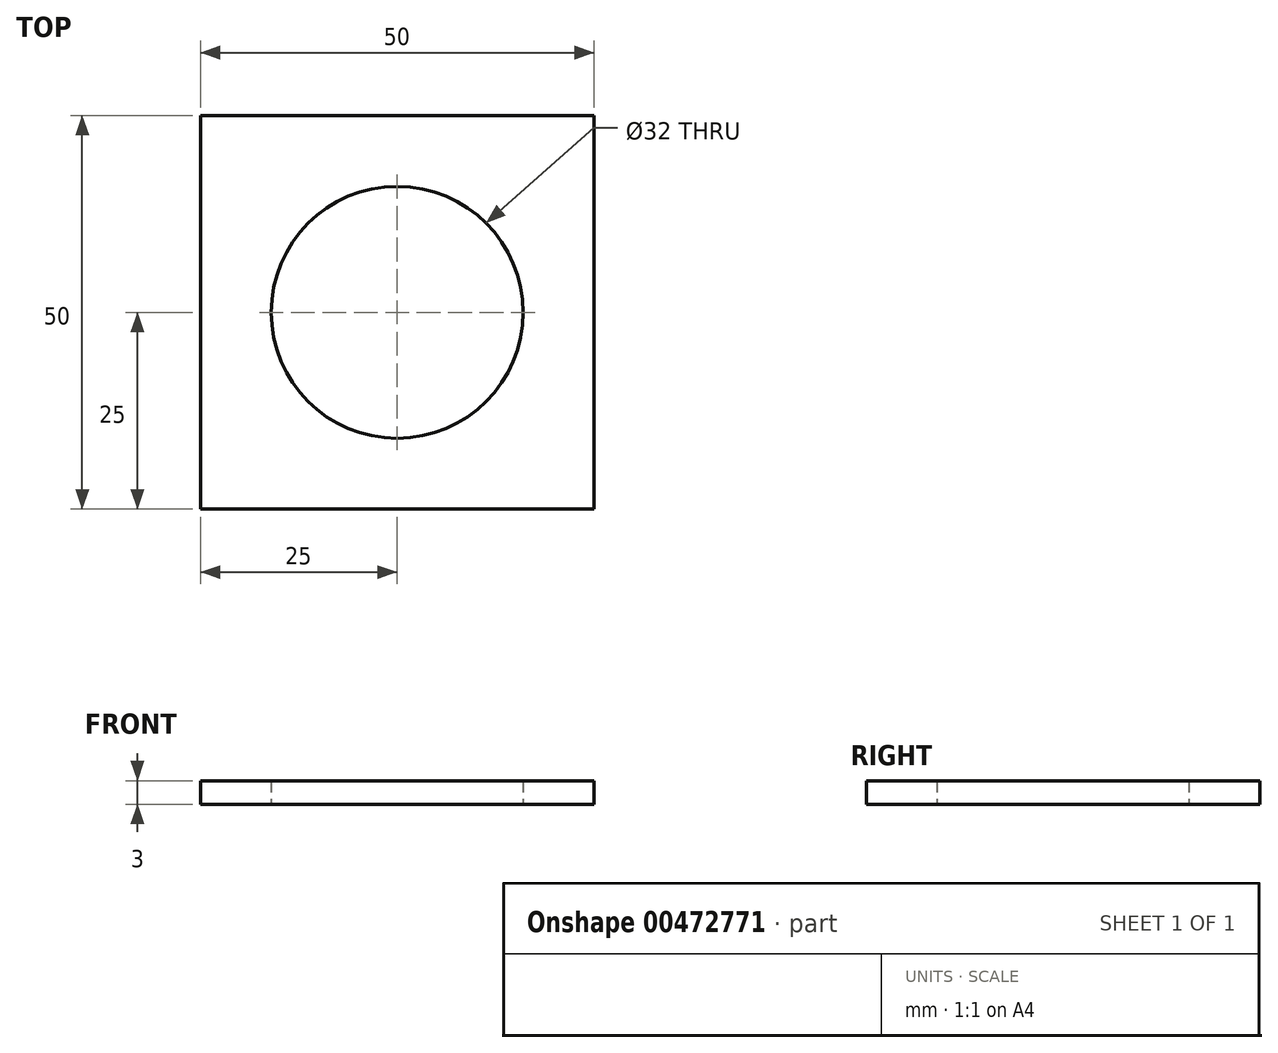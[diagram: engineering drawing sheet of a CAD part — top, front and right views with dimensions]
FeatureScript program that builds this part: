
annotation { "Feature Type Name" : "Feature", "Feature Type Description" : "" }
export const myFeature = defineFeature(function(context is Context, id is Id, definition is map)
    precondition{}
    {
        {
            assignVariable(context, id + "F0", {"name" : "e", "anyValue" : 3});
        }
        {
            var Q0;
            Q0=qCreatedBy(makeId("Top.planeOp"),FACE);
            var sketch = newSketch(context, id + "F1", { "sketchPlane" : qUnion([Q0])});
            skLineSegment(sketch, "E0.bottom", {"start": v(25, 25) * mm, "end": v(-25, 25) * mm});
            skLineSegment(sketch, "E0.top", {"start": v(25, -25) * mm, "end": v(-25, -25) * mm});
            skLineSegment(sketch, "E0.left", {"start": v(25, 25) * mm, "end": v(25, -25) * mm});
            skLineSegment(sketch, "E0.right", {"start": v(-25, 25) * mm, "end": v(-25, -25) * mm});
            skPoint(sketch, "E0.middle", {"position": v(0, 0) * mm});
            skCircle(sketch, "E1", {"center": v(0, 0) * mm, "radius": 16 * mm});
            skSolve(sketch);
        }
        {
            var Q0;
            Q0=makeQuery(id+"F1.imprint","IMPRINT",FACE,{"disambiguationData":[TD([[makeQuery(id+"F1.imprint","IMPRINT",EDGE,{"derivedFrom":sQuery(id+"F1.wireOp",EDGE,"E0.bottom")}),1.0]])]});
            extrude(context, id + "F2", {"entities" : qUnion([Q0]), "depth" : getVariable(context, 'e') * mm, "offsetDistance" : 25 * mm});
        }
    });
